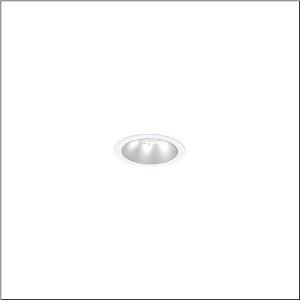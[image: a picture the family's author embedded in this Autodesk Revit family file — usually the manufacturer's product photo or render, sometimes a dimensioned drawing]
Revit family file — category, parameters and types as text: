
# Revit family: lunis_21_s_51db19ea91c
name_source: partatom
category: Lighting Fixtures
units: mm (PartAtom-declared; Revit-internal decimal feet)

## family parameters
Cut with Voids When Loaded = No
Host = Face
Light Source = No
Part Type = Normal
Room Calculation Point = No
Round Connector Dimension = Use Diameter
Shared = No

## types (1)
- --- (1 x LED, 1190 lm, 8 W, 6500K)
    Apparent Load = 8 VA
    CIE Flux Codes = 90 98 100 100 100
    Color Rendering = 80
    Color Temperature = 6500K
    Default Elevation = 1800 mm
    Description = Lunis 21 S, downlight, light control with lens, of PMMA, anti glare with reflector, of PC, matt, light emission: direct distribution, LED rated luminous flux: 910lm, light colour: 830/840/865, with terminal, 5-pole, mains connection: 220..240V, AC, 50..60Hz, housing, round, of diecast aluminium, traffic white (RAL 9016), diameter: 84mm, clamping range: 1..40mm, protection rating (complete): IP20, protection rating (on room side): IP54, insulation class (complete): insulation class II (safety insulation), certification: CE, impact resistance: IK03, packaging unit: 1 piece
    Height = 0 mm  [stored 0 ft]
    Lamp = 1 x LED
    Lamp Light Flux = 1190 lm
    Lamp Power = 8 W
    Lamp count = 1
    Length = 84 mm
    Luminous efficacy = 149 lm/W
    Manufacturer = Siteco
    ModVariant = No
    Model = 51DB19EA91C
    Mounting Place = Ceiling
    Mounting Type = Recessed
    Number of Poles = 1
    OnlyDefault = Yes
    Power Factor = 1
    Product Name = Lunis 21 S
    Product group = downlight
    ProductGroupID = 401
    Protection Class = Protection class II
    Protection Degree = IP 20
    RLX_Detail_Level = 1
    RLX_Emergency_Light_Flux = 0 lm
    RLX_Emergency_Type = 0
    RLX_Emergency_Type_DB = No
    RlxData = <blob elided: 9613 chars, md5=f19face1>
    Socket = socket
    Standby Power = 0 W
    System Light Flux = 1190 lm
    System Power = 8 W
    Type Comments = individual setting: colour temperature 6500K, luminous flux: 100 % | (OFF | OFF | ON | OFF) | 200 mA
    Type Image = l_1290846.jpg
    URL = http://relux.com
    VarID = @adj_035039
    Voltage = 0 V
    Weight = 0.00 kg
    Width = 0 mm  [stored 0 ft]

note: [stored X ft] marks values corroborated as IEEE doubles in the binary element streams (Revit-internal decimal feet)

## geometry (parser evidence)
native form markers: Sweep x7
no freeform markers — native parametric forms only
